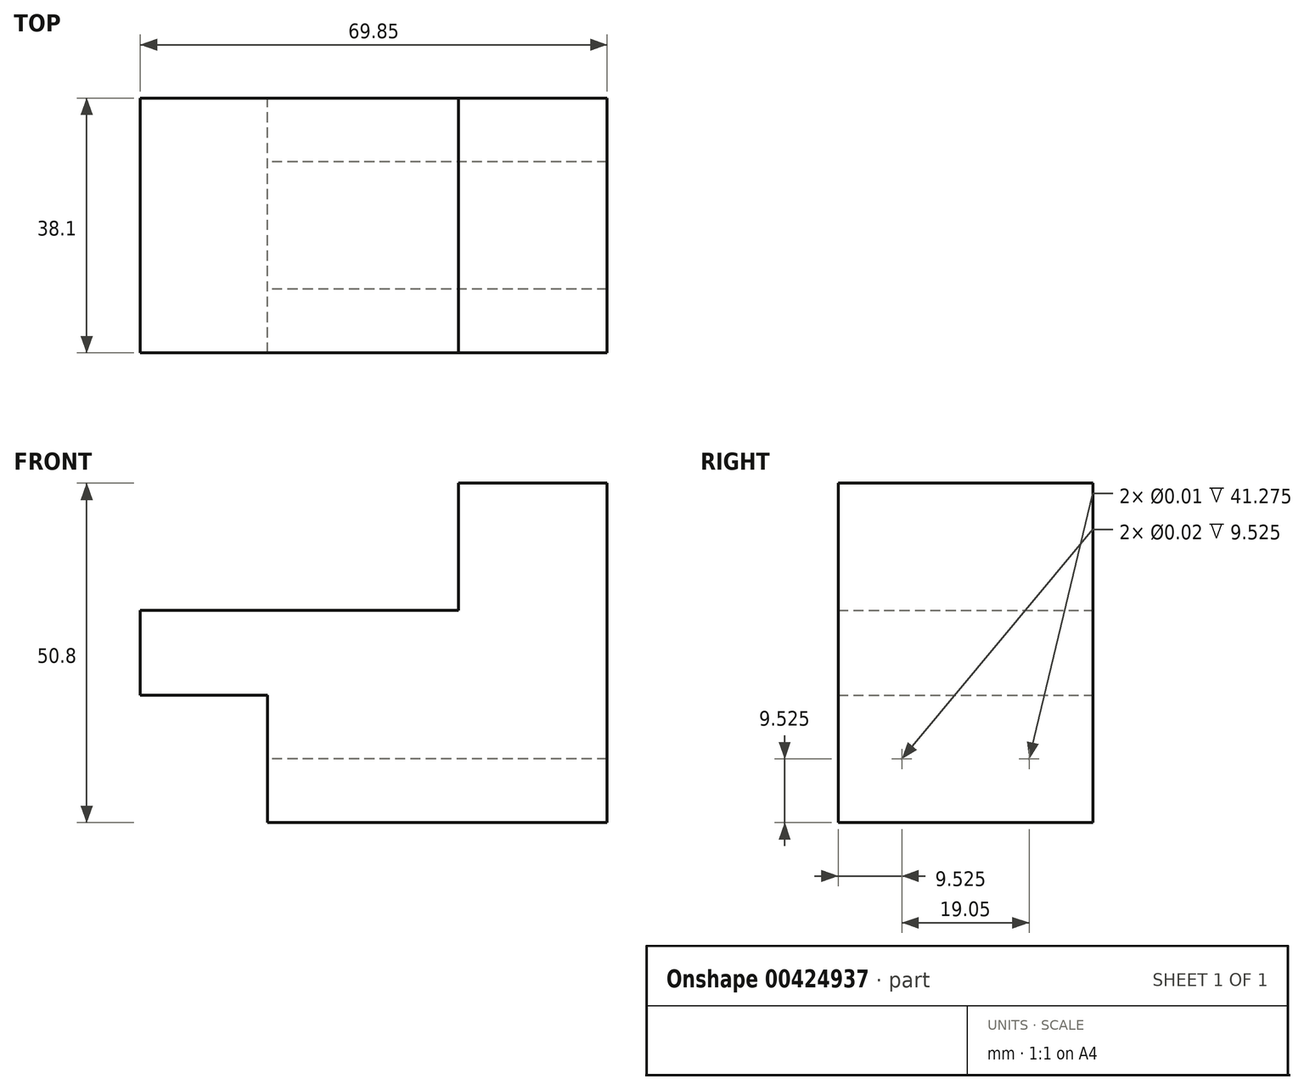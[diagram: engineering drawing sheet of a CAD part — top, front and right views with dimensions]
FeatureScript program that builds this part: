
annotation { "Feature Type Name" : "Feature", "Feature Type Description" : "" }
export const myFeature = defineFeature(function(context is Context, id is Id, definition is map)
    precondition{}
    {
        {
            var Q0;
            Q0=qCreatedBy(makeId("Front.planeOp"),FACE);
            var sketch = newSketch(context, id + "F0", { "sketchPlane" : qUnion([Q0])});
            skLineSegment(sketch, "E0", {"start": v(0, 0) * mm, "end": v(-50.8, 0) * mm});
            skLineSegment(sketch, "E1", {"start": v(-50.8, 0) * mm, "end": v(-50.8, 19.05) * mm});
            skLineSegment(sketch, "E2", {"start": v(-50.8, 19.05) * mm, "end": v(-69.85, 19.05) * mm});
            skLineSegment(sketch, "E3", {"start": v(-69.85, 19.05) * mm, "end": v(-69.85, 31.75) * mm});
            skLineSegment(sketch, "E4", {"start": v(-69.85, 31.75) * mm, "end": v(-22.22, 31.75) * mm});
            skLineSegment(sketch, "E5", {"start": v(-22.22, 31.75) * mm, "end": v(-22.23, 50.8) * mm});
            skLineSegment(sketch, "E6", {"start": v(-22.23, 50.8) * mm, "end": v(0, 50.8) * mm});
            skLineSegment(sketch, "E7", {"start": v(0, 50.8) * mm, "end": v(0, 0) * mm});
            skSolve(sketch);
        }
        {
            var Q0;
            Q0=makeQuery(id+"F0.imprint","IMPRINT",FACE,{"disambiguationData":[TD([[makeQuery(id+"F0.imprint","IMPRINT",EDGE,{"derivedFrom":sQuery(id+"F0.wireOp",EDGE,"E0")}),-1.0]])]});
            extrude(context, id + "F1", {"entities" : qUnion([Q0]), "depth" : 38.1 * mm, "symmetric" : true});
        }
        {
            var Q0;
            Q0=makeQuery(id+"F1.opExtrude","SWEPT_FACE",FACE,{"disambiguationData":[OSD([sQuery(id+"F0.wireOp",EDGE,"E7")])]});
            var sketch = newSketch(context, id + "F2", { "sketchPlane" : qUnion([Q0])});
            skLineSegment(sketch, "E8", {"start": v(19.05, 9.53) * mm, "end": v(-19.05, 9.52) * mm, "construction": true});
            skPoint(sketch, "E9", {"position": v(-9.53, 9.52) * mm});
            skPoint(sketch, "E10", {"position": v(9.53, 9.52) * mm});
            skSolve(sketch);
        }
        {
            var Q0;
            Q0=sQuery(id+"F2.wireOp",VERTEX,"E9");
            var Q1;
            Q1=sQuery(id+"F2.wireOp",VERTEX,"E10");
            var Q2;
            Q2=makeQuery(id+"F1.opExtrude","SWEPT_BODY",BODY,{"disambiguationData":[OSD([sQuery(id+"F0.wireOp",EDGE,"E0"),sQuery(id+"F0.wireOp",EDGE,"E1"),sQuery(id+"F0.wireOp",EDGE,"E2"),sQuery(id+"F0.wireOp",EDGE,"E3"),sQuery(id+"F0.wireOp",EDGE,"E4"),sQuery(id+"F0.wireOp",EDGE,"E5"),sQuery(id+"F0.wireOp",EDGE,"E6"),sQuery(id+"F0.wireOp",EDGE,"E7")])]});
            hole(context, id + "F3", {"style" : HoleStyle.C_BORE, "endStyle" : HoleEndStyle.THROUGH, "standardTappedOrClearance" : lookupTablePath({ "standard" : "ANSI", "size" : "3/8 (0.38)", "type" : "Drilled" }), "standardBlindInLast" : lookupTablePath({ "standard" : "ANSI", "size" : "3/8", "type" : "Drilled" }), "holeDiameter" : 3 / 203.2 * mm, "cBoreDiameter" : 5 / 203.2 * mm, "cBoreDepth" : 9.52 * mm, "isTappedThrough" : true, "tappedDepth" : 29.3 * mm, "tapClearance" : 3, "locations" : qUnion([Q0, Q1]), "scope" : qUnion([Q2]), "startStyle" : HoleStartStyle.SKETCH});
        }
    });
